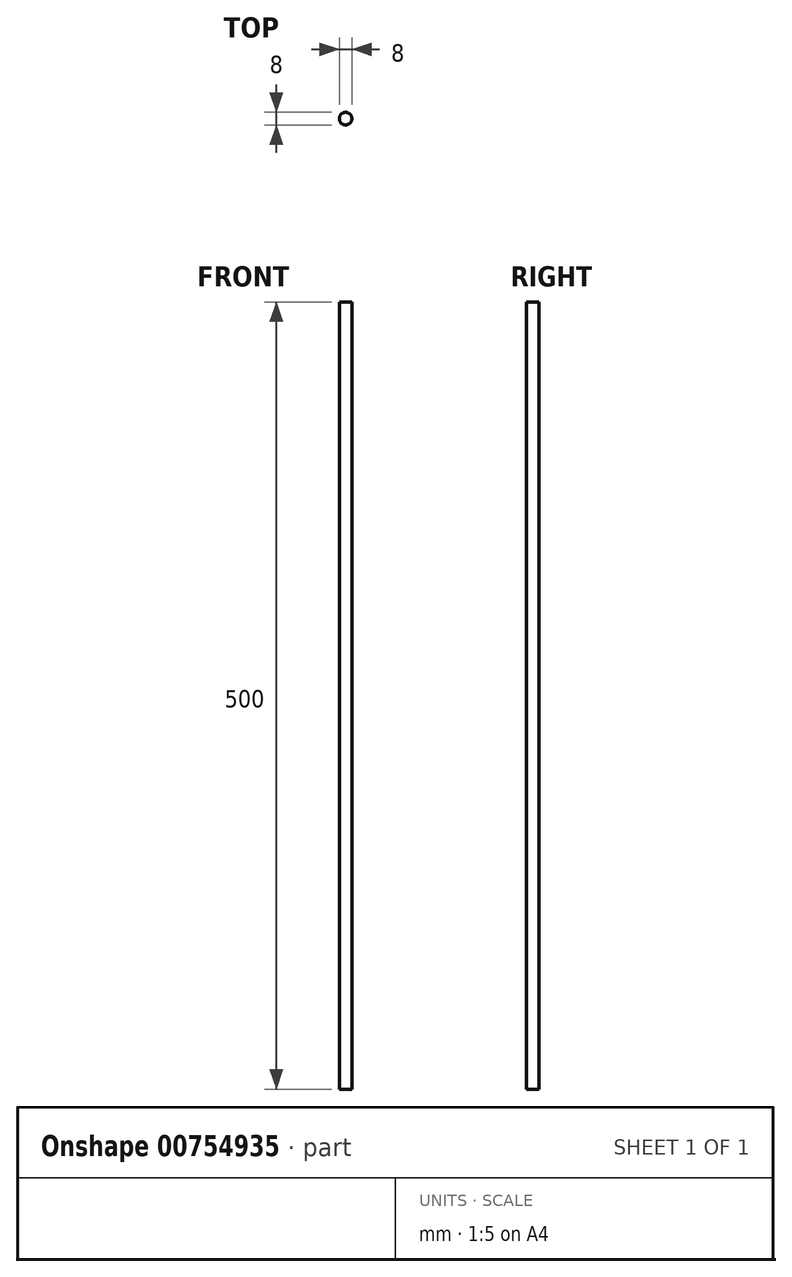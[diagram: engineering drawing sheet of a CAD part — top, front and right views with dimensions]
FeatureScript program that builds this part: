
annotation { "Feature Type Name" : "Feature", "Feature Type Description" : "" }
export const myFeature = defineFeature(function(context is Context, id is Id, definition is map)
    precondition{}
    {
        {
            var Q0;
            Q0=qCreatedBy(makeId("Top.planeOp"),FACE);
            var sketch = newSketch(context, id + "F0", { "sketchPlane" : qUnion([Q0])});
            skCircle(sketch, "E0", {"center": v(0, 0) * mm, "radius": 4 * mm});
            skSolve(sketch);
        }
        {
            var Q0;
            Q0=makeQuery(id+"F0.imprint","IMPRINT",FACE,{"disambiguationData":[TD([[makeQuery(id+"F0.imprint","IMPRINT",EDGE,{"derivedFrom":sQuery(id+"F0.wireOp",EDGE,"E0")}),1.0]])]});
            extrude(context, id + "F1", {"entities" : qUnion([Q0]), "depth" : 500 * mm, "offsetDistance" : 25 * mm});
        }
    });
